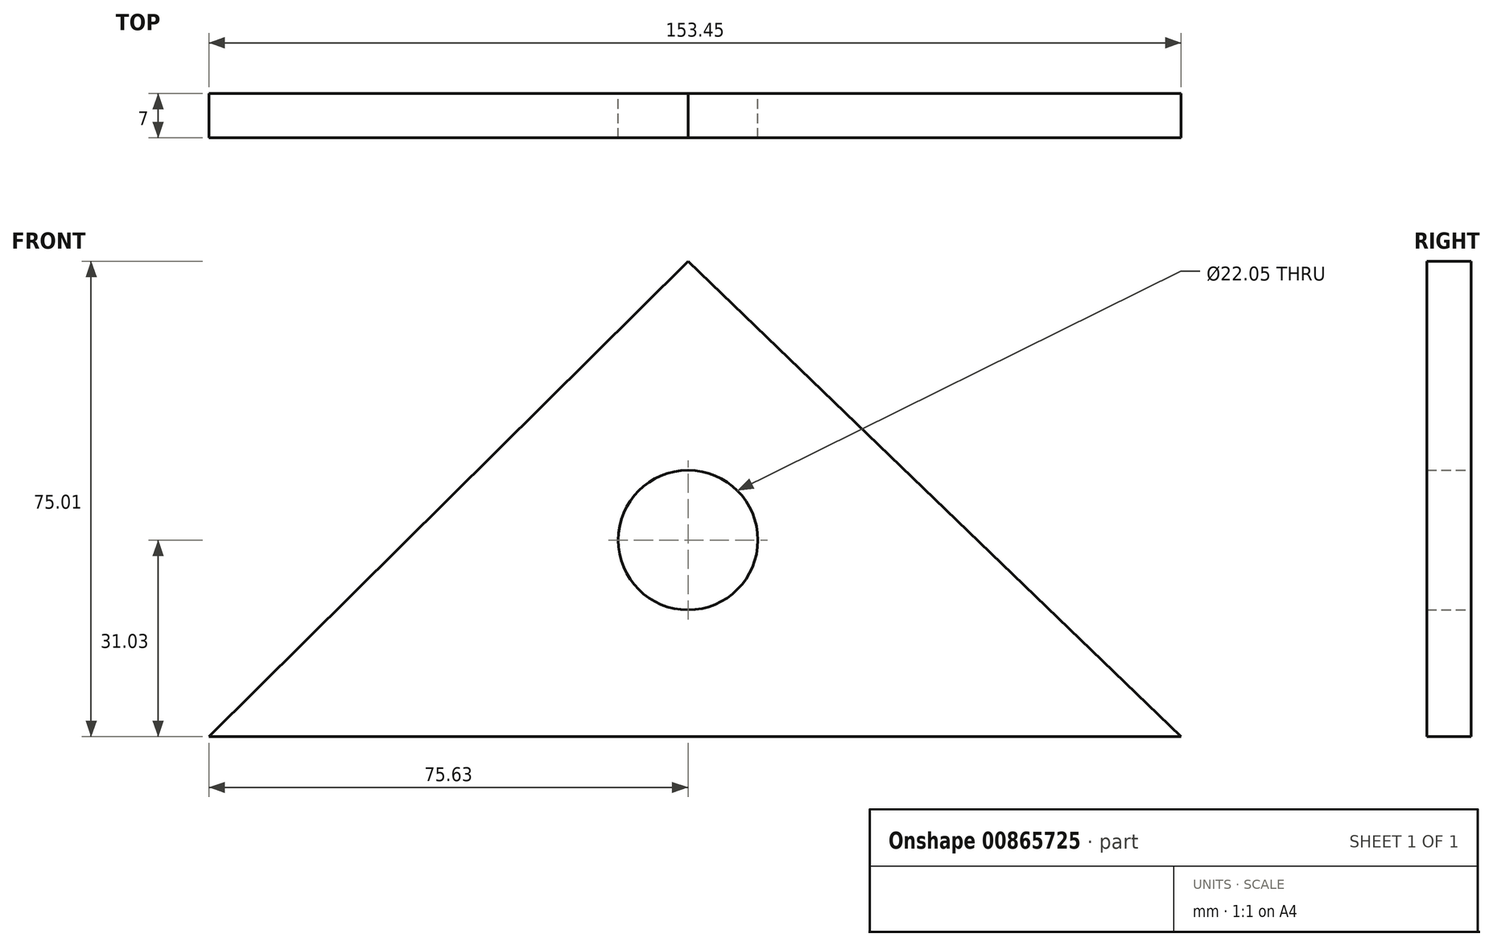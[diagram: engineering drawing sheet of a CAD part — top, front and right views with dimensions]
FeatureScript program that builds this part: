
annotation { "Feature Type Name" : "Feature", "Feature Type Description" : "" }
export const myFeature = defineFeature(function(context is Context, id is Id, definition is map)
    precondition{}
    {
        {
            var Q0;
            Q0=qCreatedBy(makeId("Front.planeOp"),FACE);
            var sketch = newSketch(context, id + "F0", { "sketchPlane" : qUnion([Q0])});
            skCircle(sketch, "E0", {"center": v(0, 0) * mm, "radius": 16.02 * mm});
            skCircle(sketch, "E1", {"center": v(0, 0) * mm, "radius": 11.03 * mm});
            skLineSegment(sketch, "E2", {"start": v(0, -31.03) * mm, "end": v(-20, -31.03) * mm});
            skLineSegment(sketch, "E3", {"start": v(0, -31.03) * mm, "end": v(20, -31.02) * mm});
            skLineSegment(sketch, "E4", {"start": v(-20, -31.03) * mm, "end": v(-52.7, -31.03) * mm});
            skLineSegment(sketch, "E5", {"start": v(-52.7, -31.03) * mm, "end": v(54.88, -31.03) * mm});
            skLineSegment(sketch, "E6", {"start": v(-52.7, -31.03) * mm, "end": v(0, 31.03) * mm});
            skLineSegment(sketch, "E7", {"start": v(54.88, -31.03) * mm, "end": v(0, 31.03) * mm});
            skLineSegment(sketch, "E8", {"start": v(-52.7, -31.03) * mm, "end": v(-75.63, -31.03) * mm});
            skLineSegment(sketch, "E9", {"start": v(-75.63, -31.03) * mm, "end": v(-52.7, -31.03) * mm});
            skLineSegment(sketch, "E10", {"start": v(54.88, -31.03) * mm, "end": v(77.82, -31.03) * mm});
            skLineSegment(sketch, "E11", {"start": v(77.82, -31.03) * mm, "end": v(0, 43.98) * mm});
            skLineSegment(sketch, "E12", {"start": v(0, 43.98) * mm, "end": v(-75.63, -31.03) * mm});
            skLineSegment(sketch, "E13", {"start": v(-75.63, -31.03) * mm, "end": v(-52.7, -48.28) * mm});
            skLineSegment(sketch, "E14", {"start": v(54.88, -48.28) * mm, "end": v(-52.7, -48.28) * mm});
            skLineSegment(sketch, "E15", {"start": v(77.82, -31.02) * mm, "end": v(54.88, -48.28) * mm});
            skSolve(sketch);
        }
        {
            var Q0;
            Q0=makeQuery(id+"F0.imprint","IMPRINT",FACE,{"disambiguationData":[TD([[makeQuery(id+"F0.imprint","IMPRINT",EDGE,{"derivedFrom":sQuery(id+"F0.wireOp",EDGE,"E6")}),1.0]])]});
            var Q1;
            Q1=makeQuery(id+"F0.imprint","IMPRINT",FACE,{"disambiguationData":[TD([[makeQuery(id+"F0.imprint","IMPRINT",EDGE,{"derivedFrom":sQuery(id+"F0.wireOp",EDGE,"E0")}),1.0]])]});
            var Q2;
            Q2=makeQuery(id+"F0.imprint","IMPRINT",FACE,{"disambiguationData":[TD([[makeQuery(id+"F0.imprint","IMPRINT",EDGE,{"derivedFrom":sQuery(id+"F0.wireOp",EDGE,"E0")}),-1.0]])]});
            var Q3;
            {var subQ0=sQuery(id+"F0.wireOp",EDGE,"E9");Q3=makeQuery(id+"F0.imprint","IMPRINT",FACE,{"disambiguationData":[TD([[makeQuery(id+"F0.imprint","IMPRINT",EDGE,{"derivedFrom":subQ0}),-1.0]])]});}
            extrude(context, id + "F1", {"entities" : qUnion([Q0, Q1, Q2, Q3]), "depth" : 7 * mm, "offsetDistance" : 25 * mm});
        }
    });
